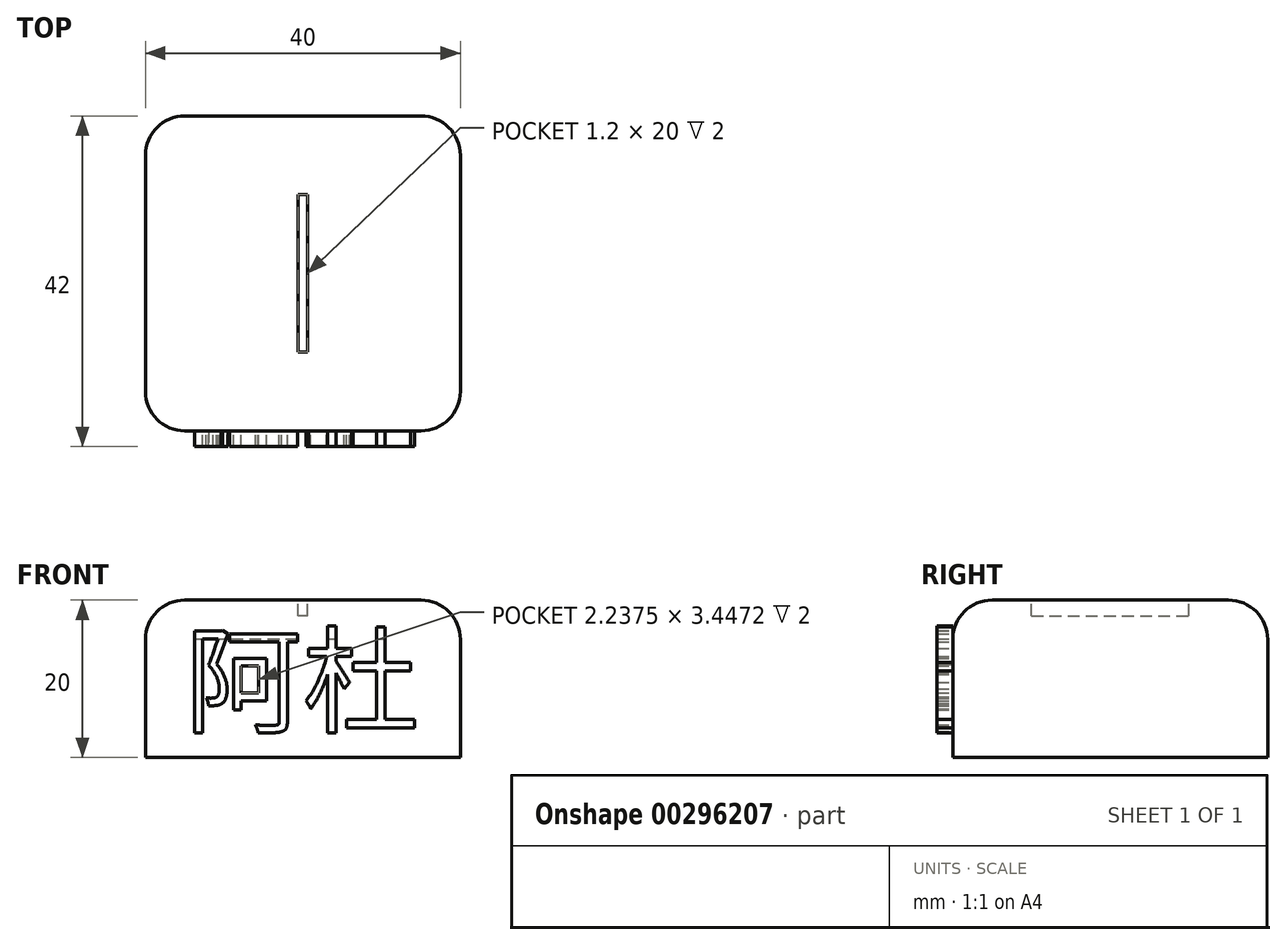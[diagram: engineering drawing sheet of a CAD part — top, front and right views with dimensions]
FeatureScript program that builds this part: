
annotation { "Feature Type Name" : "Feature", "Feature Type Description" : "" }
export const myFeature = defineFeature(function(context is Context, id is Id, definition is map)
    precondition{}
    {
        {
            var Q0;
            Q0=qCreatedBy(makeId("Top.planeOp"),FACE);
            var sketch = newSketch(context, id + "F0", { "sketchPlane" : qUnion([Q0])});
            skLineSegment(sketch, "E0.bottom", {"start": v(20, -20) * mm, "end": v(-20, -20) * mm});
            skLineSegment(sketch, "E0.top", {"start": v(20, 20) * mm, "end": v(-20, 20) * mm});
            skLineSegment(sketch, "E0.left", {"start": v(20, -20) * mm, "end": v(20, 20) * mm});
            skLineSegment(sketch, "E0.right", {"start": v(-20, -20) * mm, "end": v(-20, 20) * mm});
            skPoint(sketch, "E0.middle", {"position": v(0, 0) * mm});
            skLineSegment(sketch, "E1.bottom", {"start": v(0.6, -10) * mm, "end": v(-0.6, -10) * mm});
            skLineSegment(sketch, "E1.top", {"start": v(0.6, 10) * mm, "end": v(-0.6, 10) * mm});
            skLineSegment(sketch, "E1.left", {"start": v(0.6, -10) * mm, "end": v(0.6, 10) * mm});
            skLineSegment(sketch, "E1.right", {"start": v(-0.6, -10) * mm, "end": v(-0.6, 10) * mm});
            skSolve(sketch);
        }
        {
            var Q0;
            Q0=makeQuery(id+"F0.imprint","IMPRINT",FACE,{"disambiguationData":[TD([[makeQuery(id+"F0.imprint","IMPRINT",EDGE,{"derivedFrom":sQuery(id+"F0.wireOp",EDGE,"E0.bottom")}),-1.0]])]});
            var Q1;
            Q1=makeQuery(id+"F0.imprint","IMPRINT",FACE,{"disambiguationData":[TD([[makeQuery(id+"F0.imprint","IMPRINT",EDGE,{"derivedFrom":sQuery(id+"F0.wireOp",EDGE,"E1.bottom")}),-1.0]])]});
            extrude(context, id + "F1", {"entities" : qUnion([Q0, Q1]), "oppositeDirection" : true, "depth" : 20 * mm});
        }
        {
            var Q0;
            Q0=makeQuery(id+"F0.imprint","IMPRINT",FACE,{"disambiguationData":[TD([[makeQuery(id+"F0.imprint","IMPRINT",EDGE,{"derivedFrom":sQuery(id+"F0.wireOp",EDGE,"E1.bottom")}),-1.0]])]});
            extrude(context, id + "F2", {"entities" : qUnion([Q0]), "operationType" : NewBodyOperationType.REMOVE, "oppositeDirection" : true, "depth" : 2 * mm});
        }
        {
            var Q0;
            Q0=makeQuery(id+"F2.boolean.opBoolean","COPY",EDGE,{"derivedFrom":makeQuery(id+"F2.opExtrude","CAP_EDGE",EDGE,{"disambiguationData":[OSD([sQuery(id+"F0.wireOp",EDGE,"E1.left")])],"isStart":true})});
            var Q1;
            Q1=makeQuery(id+"F2.boolean.opBoolean","COPY",EDGE,{"derivedFrom":makeQuery(id+"F2.opExtrude","CAP_EDGE",EDGE,{"disambiguationData":[OSD([sQuery(id+"F0.wireOp",EDGE,"E1.right")])],"isStart":true})});
            var Q2;
            Q2=makeQuery(id+"F1.opExtrude","SWEPT_EDGE",EDGE,{"disambiguationData":[OSD([sQuery(id+"F0.wireOp",EDGE,"E0.bottom"),sQuery(id+"F0.wireOp",EDGE,"E0.left")])]});
            var Q3;
            Q3=makeQuery(id+"F1.opExtrude","SWEPT_EDGE",EDGE,{"disambiguationData":[OSD([sQuery(id+"F0.wireOp",EDGE,"E0.top"),sQuery(id+"F0.wireOp",EDGE,"E0.left")])]});
            var Q4;
            Q4=makeQuery(id+"F1.opExtrude","CAP_EDGE",EDGE,{"disambiguationData":[OSD([sQuery(id+"F0.wireOp",EDGE,"E0.left")])],"isStart":true});
            var Q5;
            Q5=makeQuery(id+"F1.opExtrude","SWEPT_EDGE",EDGE,{"disambiguationData":[OSD([sQuery(id+"F0.wireOp",EDGE,"E0.bottom"),sQuery(id+"F0.wireOp",EDGE,"E0.right")])]});
            var Q6;
            Q6=makeQuery(id+"F1.opExtrude","SWEPT_EDGE",EDGE,{"disambiguationData":[OSD([sQuery(id+"F0.wireOp",EDGE,"E0.top"),sQuery(id+"F0.wireOp",EDGE,"E0.right")])]});
            var Q7;
            Q7=makeQuery(id+"F1.opExtrude","CAP_EDGE",EDGE,{"disambiguationData":[OSD([sQuery(id+"F0.wireOp",EDGE,"E0.top")])],"isStart":true});
            var Q8;
            Q8=makeQuery(id+"F1.opExtrude","CAP_EDGE",EDGE,{"disambiguationData":[OSD([sQuery(id+"F0.wireOp",EDGE,"E0.right")])],"isStart":true});
            var Q9;
            Q9=makeQuery(id+"F1.opExtrude","CAP_EDGE",EDGE,{"disambiguationData":[OSD([sQuery(id+"F0.wireOp",EDGE,"E0.bottom")])],"isStart":true});
            fillet(context, id + "F3", {"entities" : qUnion([Q0, Q1, Q2, Q3, Q4, Q5, Q6, Q7, Q8, Q9]), "radius" : 5 * mm, "tangentPropagation" : true, "allowEdgeOverflow" : false});
        }
        {
            var Q0;
            Q0=makeQuery(id+"F1.opExtrude","SWEPT_FACE",FACE,{"disambiguationData":[OSD([sQuery(id+"F0.wireOp",EDGE,"E0.bottom")])]});
            var sketch = newSketch(context, id + "F4", { "sketchPlane" : qUnion([Q0])});
            skText(sketch, "E2", { "text": "阿杜", "fontName": "NotoSansCJKtc-Regular.otf"});
            const initialGuessF4  = {"E2": [-0.015, -0.01574, 1, 0, 0.01074]};
            skSetInitialGuess(sketch, initialGuessF4);
            skSolve(sketch);
        }
        {
            var Q0;
            {var subQ1=sQuery(id+"F4.wireOp",EDGE,"E2.sketch_text.stroke-30");Q0=makeQuery(id+"F4.imprint","IMPRINT",FACE,{"disambiguationData":[TD([[makeQuery(id+"F4.imprint","IMPRINT",EDGE,{"derivedFrom":subQ1}),1.0]])]});}
            var Q1;
            {var subQ0=sQuery(id+"F4.wireOp",EDGE,"E2.sketch_text.stroke-28");Q1=makeQuery(id+"F4.imprint","IMPRINT",FACE,{"disambiguationData":[TD([[makeQuery(id+"F4.imprint","IMPRINT",EDGE,{"derivedFrom":subQ0}),1.0]])]});}
            var Q2;
            Q2=makeQuery(id+"F4.imprint","IMPRINT",FACE,{"disambiguationData":[TD([[makeQuery(id+"F4.imprint","IMPRINT",EDGE,{"derivedFrom":sQuery(id+"F4.wireOp",EDGE,"E2.sketch_text.stroke-0")}),1.0]])]});
            var Q3;
            {var subQ1=sQuery(id+"F4.wireOp",EDGE,"E2.sketch_text.stroke-7");Q3=makeQuery(id+"F4.imprint","IMPRINT",FACE,{"disambiguationData":[TD([[makeQuery(id+"F4.imprint","IMPRINT",EDGE,{"derivedFrom":subQ1}),1.0]])]});}
            var Q4;
            {var subQ0=sQuery(id+"F4.wireOp",EDGE,"E2.sketch_text.stroke-3");Q4=makeQuery(id+"F4.imprint","IMPRINT",FACE,{"disambiguationData":[TD([[makeQuery(id+"F4.imprint","IMPRINT",EDGE,{"derivedFrom":subQ0}),1.0]])]});}
            var Q5;
            Q5=makeQuery(id+"F4.imprint","IMPRINT",FACE,{"disambiguationData":[TD([[makeQuery(id+"F4.imprint","IMPRINT",EDGE,{"derivedFrom":sQuery(id+"F4.wireOp",EDGE,"E2.sketch_text.stroke-18")}),1.0]])]});
            var Q6;
            Q6=makeQuery(id+"F4.imprint","IMPRINT",FACE,{"disambiguationData":[TD([[makeQuery(id+"F4.imprint","IMPRINT",EDGE,{"derivedFrom":sQuery(id+"F4.wireOp",EDGE,"E2.sketch_text.stroke-40")}),1.0]])]});
            var Q7;
            {var subQ0=sQuery(id+"F4.wireOp",EDGE,"E2.sketch_text.stroke-46");Q7=makeQuery(id+"F4.imprint","IMPRINT",FACE,{"disambiguationData":[TD([[makeQuery(id+"F4.imprint","IMPRINT",EDGE,{"derivedFrom":subQ0}),1.0]])]});}
            var Q8;
            {var subQ0=sQuery(id+"F4.wireOp",EDGE,"E2.sketch_text.stroke-64");Q8=makeQuery(id+"F4.imprint","IMPRINT",FACE,{"disambiguationData":[TD([[makeQuery(id+"F4.imprint","IMPRINT",EDGE,{"derivedFrom":subQ0}),1.0]])]});}
            var Q9;
            Q9=makeQuery(id+"F4.imprint","IMPRINT",FACE,{"disambiguationData":[TD([[makeQuery(id+"F4.imprint","IMPRINT",EDGE,{"derivedFrom":sQuery(id+"F4.wireOp",EDGE,"E2.sketch_text.stroke-59")}),1.0]])]});
            extrude(context, id + "F5", {"entities" : qUnion([Q0, Q1, Q2, Q3, Q4, Q5, Q6, Q7, Q8, Q9]), "operationType" : NewBodyOperationType.ADD, "depth" : 2 * mm});
        }
    });
